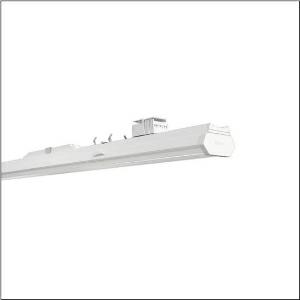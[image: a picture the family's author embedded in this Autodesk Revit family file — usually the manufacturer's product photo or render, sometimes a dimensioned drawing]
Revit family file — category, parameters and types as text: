
# Revit family: licross_r__21_protected_ho_52tp13mn4fxs_ad58
name_source: partatom
category: Lighting Fixtures
units: mm (PartAtom-declared; Revit-internal decimal feet)

## family parameters
Cut with Voids When Loaded = No
Host = Face
Light Source = No
Part Type = Normal
Room Calculation Point = No
Round Connector Dimension = Use Diameter
Shared = No

## types (1)
- --- (1 x LED, 15060 lm, 83.2 W, 4000K)
    Apparent Load = 83 VA
    CIE Flux Codes = 89 96 99 100 99
    Color Rendering = 80
    Color Temperature = 4000K
    Default Elevation = 1800 mm
    Description = Licross® 21 Protected HO, luminaire insert, of sheet steel, galvanised, coil coated, white, length: 1.500mm, width: 66mm, height: 67mm, LED rated luminous flux: 15.060lm, light colour: 840, control gear: ON/OFF Multilumen, with plug, 3-pole, with phase selection, mains connection: 220..240V, AC, 50/60Hz, rated input power: 83W, internal wiring halogen-free, primary light control with lens, of plastic, primary optical cover: cover, of PMMA, light emission: direct distribution, primary light characteristic: symmetric, protection rating (complete): IP64, insulation class (complete): insulation class I (protective earthing), certification: CE, ENEC, VDE, UKCA, protection symbol: D if used in an environment with conductive dust loads with corresponding accessories, impact resistance: IK06, permissible ambient temperature for indoor applications: -35..+35°C, corresponds to IFS (International Featured Standards) requirements for safety and quality in the food industry, reducing of maximum allowable ambient temperature of 5°C with ceiling mounting, LABS conformity tested according to VDMA 24364:2018-05, packaging unit: 1 piece
    Height = 92 mm
    Lamp = 1 x LED
    Lamp Light Flux = 15060 lm
    Lamp Power = 83.2 W
    Lamp count = 1
    Length = 1500 mm
    Luminous efficacy = 181 lm/W
    Manufacturer = Siteco
    ModVariant = No
    Model = 52TP13MN4FXS
    Mounting Place = Ceiling
    Mounting Type = Pendant
    Number of Poles = 1
    OnlyDefault = Yes
    Power Factor = 1
    Product Name = Licross® 21 Protected HO
    Product group = luminaire insert | ceiling pendant
    ProductGroupID = 902
    Protection Class = Protection class I
    Protection Degree = IP 64
    RLX_Detail_Level = 1
    RLX_Emergency_Light_Flux = 0 lm
    RLX_Emergency_Type = 0
    RLX_Emergency_Type_DB = No
    RlxData = <blob elided: 21873 chars, md5=5738a728>
    Socket = socket
    Standby Power = 0 W
    System Light Flux = 15060 lm
    System Power = 83 W
    Type Comments = factory setting: luminous flux: 100 % | (A | C | E) | 195 mA
    Type Image = l_1256148.jpg
    URL = http://relux.com
    VarID = @adj_130463
    Voltage = 0 V
    Weight = 0.00 kg
    Width = 88 mm

## geometry (parser evidence)
native form markers: Blend x4, Sweep x12
no freeform markers — native parametric forms only
